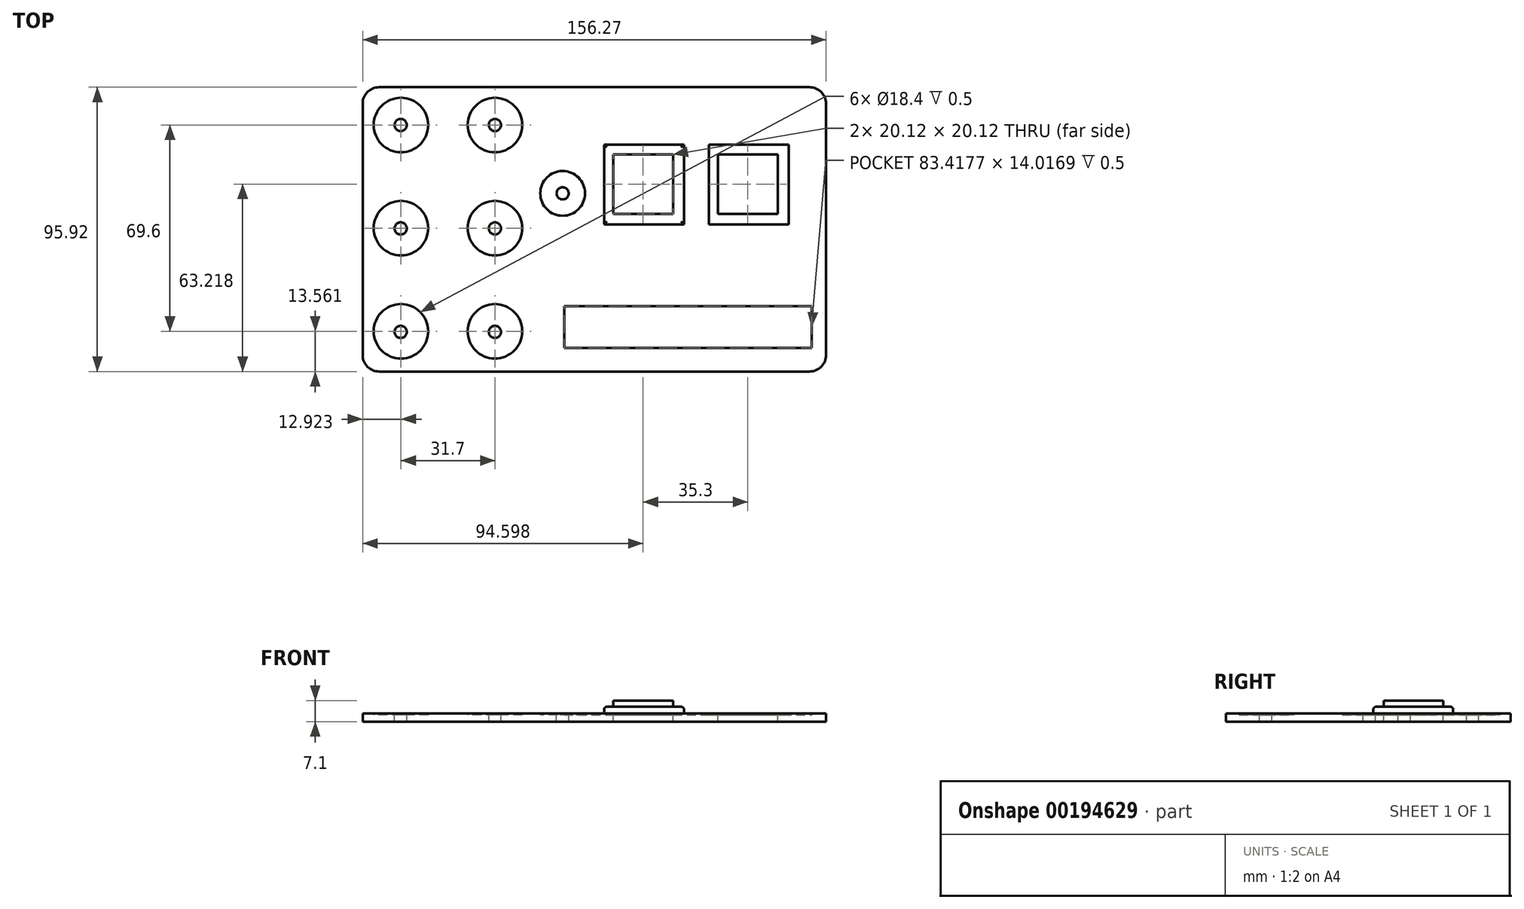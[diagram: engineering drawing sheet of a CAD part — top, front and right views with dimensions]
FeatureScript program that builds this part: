
annotation { "Feature Type Name" : "Feature", "Feature Type Description" : "" }
export const myFeature = defineFeature(function(context is Context, id is Id, definition is map)
    precondition{}
    {
        {
            var Q0;
            Q0=qCreatedBy(makeId("Top.planeOp"),FACE);
            var sketch = newSketch(context, id + "F0", { "sketchPlane" : qUnion([Q0])});
            skLineSegment(sketch, "E0.bottom", {"start": v(10.04, -4.66) * mm, "end": v(155.11, -4.66) * mm});
            skLineSegment(sketch, "E0.top", {"start": v(10.04, -100.58) * mm, "end": v(155.11, -100.58) * mm});
            skLineSegment(sketch, "E0.left", {"start": v(4.44, -10.26) * mm, "end": v(4.44, -94.98) * mm});
            skLineSegment(sketch, "E0.right", {"start": v(160.71, -10.26) * mm, "end": v(160.71, -94.98) * mm});
            skPoint(sketch, "E1.visualSharp", {"position": v(4.44, -4.66) * mm});
            skArc(sketch, "E1.filletArc", {"start": v(10.04, -4.66) * mm, "mid": v(6.08, -6.3) * mm, "end": v(4.44, -10.26) * mm});
            skPoint(sketch, "E2.visualSharp", {"position": v(4.44, -100.58) * mm});
            skArc(sketch, "E2.filletArc", {"start": v(4.44, -94.98) * mm, "mid": v(6.08, -98.94) * mm, "end": v(10.04, -100.58) * mm});
            skPoint(sketch, "E3.visualSharp", {"position": v(160.71, -100.58) * mm});
            skArc(sketch, "E3.filletArc", {"start": v(155.11, -100.58) * mm, "mid": v(159.07, -98.94) * mm, "end": v(160.71, -94.98) * mm});
            skPoint(sketch, "E4.visualSharp", {"position": v(160.71, -4.66) * mm});
            skArc(sketch, "E4.filletArc", {"start": v(160.71, -10.26) * mm, "mid": v(159.07, -6.3) * mm, "end": v(155.11, -4.66) * mm});
            skLineSegment(sketch, "E5.bottom", {"start": v(85.85, -50.95) * mm, "end": v(112.8, -50.95) * mm});
            skLineSegment(sketch, "E5.top", {"start": v(85.85, -24) * mm, "end": v(112.8, -24) * mm});
            skLineSegment(sketch, "E5.left", {"start": v(85.85, -50.95) * mm, "end": v(85.85, -24) * mm});
            skLineSegment(sketch, "E5.right", {"start": v(112.8, -50.95) * mm, "end": v(112.8, -24) * mm});
            skCircle(sketch, "E6", {"center": v(49.06, -17.42) * mm, "radius": 9.2 * mm});
            skPoint(sketch, "E6.first.point", {"position": v(44.08, -25.15) * mm});
            skPoint(sketch, "E6.second.point", {"position": v(45.09, -9.12) * mm});
            skPoint(sketch, "E6.third.point", {"position": v(58.27, -17.36) * mm});
            skLineSegment(sketch, "E7.bottom", {"start": v(88.98, -27.3) * mm, "end": v(109.1, -27.3) * mm});
            skLineSegment(sketch, "E7.top", {"start": v(88.98, -47.42) * mm, "end": v(109.1, -47.42) * mm});
            skLineSegment(sketch, "E7.left", {"start": v(88.98, -27.3) * mm, "end": v(88.98, -47.42) * mm});
            skLineSegment(sketch, "E7.right", {"start": v(109.1, -27.3) * mm, "end": v(109.1, -47.42) * mm});
            skLineSegment(sketch, "E8.1.0.0", {"start": v(121.15, -24) * mm, "end": v(148.1, -24) * mm});
            skLineSegment(sketch, "E8.1.0.1", {"start": v(121.15, -50.95) * mm, "end": v(121.15, -24) * mm});
            skLineSegment(sketch, "E8.1.0.2", {"start": v(121.15, -50.95) * mm, "end": v(148.1, -50.95) * mm});
            skLineSegment(sketch, "E8.1.0.3", {"start": v(148.1, -50.95) * mm, "end": v(148.1, -24) * mm});
            skLineSegment(sketch, "E8.1.0.4", {"start": v(144.4, -27.3) * mm, "end": v(144.4, -47.42) * mm});
            skLineSegment(sketch, "E8.1.0.5", {"start": v(124.28, -27.3) * mm, "end": v(144.4, -27.3) * mm});
            skLineSegment(sketch, "E8.1.0.6", {"start": v(124.28, -27.3) * mm, "end": v(124.28, -47.42) * mm});
            skLineSegment(sketch, "E8.1.0.7", {"start": v(124.28, -47.42) * mm, "end": v(144.4, -47.42) * mm});
            skLineSegment(sketch, "E8.direction1", {"start": v(85.85, -50.95) * mm, "end": v(121.15, -50.95) * mm, "construction": true});
            skCircle(sketch, "E9.0.1.0", {"center": v(49.06, -52.22) * mm, "radius": 9.2 * mm});
            skCircle(sketch, "E9.0.2.0", {"center": v(49.06, -87.02) * mm, "radius": 9.2 * mm});
            skCircle(sketch, "E9.1.0.0", {"center": v(17.36, -17.42) * mm, "radius": 9.2 * mm});
            skCircle(sketch, "E9.1.1.0", {"center": v(17.36, -52.22) * mm, "radius": 9.2 * mm});
            skCircle(sketch, "E9.1.2.0", {"center": v(17.36, -87.02) * mm, "radius": 9.2 * mm});
            skLineSegment(sketch, "E9.direction1", {"start": v(49.06, -17.42) * mm, "end": v(17.36, -17.42) * mm, "construction": true});
            skLineSegment(sketch, "E9.direction2", {"start": v(49.06, -17.42) * mm, "end": v(49.06, -52.22) * mm, "construction": true});
            skCircle(sketch, "E10", {"center": v(71.88, -40.48) * mm, "radius": 7.54 * mm});
            skPoint(sketch, "E10.first.point", {"position": v(67.34, -34.46) * mm});
            skPoint(sketch, "E10.second.point", {"position": v(72.06, -48.02) * mm});
            skPoint(sketch, "E10.third.point", {"position": v(79.37, -39.64) * mm});
            skLineSegment(sketch, "E11.bottom", {"start": v(72.42, -78.56) * mm, "end": v(155.84, -78.56) * mm});
            skLineSegment(sketch, "E11.top", {"start": v(72.42, -92.58) * mm, "end": v(155.84, -92.58) * mm});
            skLineSegment(sketch, "E11.left", {"start": v(72.42, -78.56) * mm, "end": v(72.42, -92.58) * mm});
            skLineSegment(sketch, "E11.right", {"start": v(155.84, -78.56) * mm, "end": v(155.84, -92.58) * mm});
            skLineSegment(sketch, "E12.0", {"start": v(7.94, -8.16) * mm, "end": v(157.21, -8.16) * mm});
            skLineSegment(sketch, "E12.1", {"start": v(7.94, -8.16) * mm, "end": v(7.94, -97.08) * mm});
            skLineSegment(sketch, "E12.2", {"start": v(7.94, -97.08) * mm, "end": v(157.21, -97.08) * mm});
            skLineSegment(sketch, "E12.3", {"start": v(157.21, -8.16) * mm, "end": v(157.21, -97.08) * mm});
            skCircle(sketch, "E13", {"center": v(49.06, -17.42) * mm, "radius": 2.05 * mm});
            skCircle(sketch, "E14.0.1.0", {"center": v(49.06, -52.32) * mm, "radius": 2.05 * mm});
            skCircle(sketch, "E14.0.2.0", {"center": v(49.06, -87.22) * mm, "radius": 2.05 * mm});
            skCircle(sketch, "E14.1.0.0", {"center": v(17.26, -17.42) * mm, "radius": 2.05 * mm});
            skCircle(sketch, "E14.1.1.0", {"center": v(17.26, -52.32) * mm, "radius": 2.05 * mm});
            skCircle(sketch, "E14.1.2.0", {"center": v(17.26, -87.22) * mm, "radius": 2.05 * mm});
            skLineSegment(sketch, "E14.direction1", {"start": v(49.06, -17.42) * mm, "end": v(17.26, -17.42) * mm, "construction": true});
            skLineSegment(sketch, "E14.direction2", {"start": v(49.06, -17.42) * mm, "end": v(49.06, -52.32) * mm, "construction": true});
            skCircle(sketch, "E15", {"center": v(71.88, -40.48) * mm, "radius": 2.05 * mm});
            skSolve(sketch);
        }
        {
            var Q0;
            Q0=makeQuery(id+"F0.imprint","IMPRINT",FACE,{"disambiguationData":[TD([[makeQuery(id+"F0.imprint","IMPRINT",EDGE,{"derivedFrom":sQuery(id+"F0.wireOp",EDGE,"E0.bottom")}),-1.0]])]});
            var Q1;
            Q1=makeQuery(id+"F0.imprint","IMPRINT",FACE,{"disambiguationData":[TD([[makeQuery(id+"F0.imprint","IMPRINT",EDGE,{"derivedFrom":sQuery(id+"F0.wireOp",EDGE,"E5.bottom")}),-1.0]])]});
            var Q2;
            Q2=makeQuery(id+"F0.imprint","IMPRINT",FACE,{"disambiguationData":[TD([[makeQuery(id+"F0.imprint","IMPRINT",EDGE,{"derivedFrom":sQuery(id+"F0.wireOp",EDGE,"E9.1.0.0")}),1.0]])]});
            var Q3;
            Q3=makeQuery(id+"F0.imprint","IMPRINT",FACE,{"disambiguationData":[TD([[makeQuery(id+"F0.imprint","IMPRINT",EDGE,{"derivedFrom":sQuery(id+"F0.wireOp",EDGE,"E9.1.1.0")}),1.0]])]});
            var Q4;
            Q4=makeQuery(id+"F0.imprint","IMPRINT",FACE,{"disambiguationData":[TD([[makeQuery(id+"F0.imprint","IMPRINT",EDGE,{"derivedFrom":sQuery(id+"F0.wireOp",EDGE,"E9.1.2.0")}),1.0]])]});
            var Q5;
            Q5=makeQuery(id+"F0.imprint","IMPRINT",FACE,{"disambiguationData":[TD([[makeQuery(id+"F0.imprint","IMPRINT",EDGE,{"derivedFrom":sQuery(id+"F0.wireOp",EDGE,"E9.0.2.0")}),1.0]])]});
            var Q6;
            Q6=makeQuery(id+"F0.imprint","IMPRINT",FACE,{"disambiguationData":[TD([[makeQuery(id+"F0.imprint","IMPRINT",EDGE,{"derivedFrom":sQuery(id+"F0.wireOp",EDGE,"E9.0.1.0")}),1.0]])]});
            var Q7;
            Q7=makeQuery(id+"F0.imprint","IMPRINT",FACE,{"disambiguationData":[TD([[makeQuery(id+"F0.imprint","IMPRINT",EDGE,{"derivedFrom":sQuery(id+"F0.wireOp",EDGE,"E6")}),1.0]])]});
            var Q8;
            Q8=makeQuery(id+"F0.imprint","IMPRINT",FACE,{"disambiguationData":[TD([[makeQuery(id+"F0.imprint","IMPRINT",EDGE,{"derivedFrom":sQuery(id+"F0.wireOp",EDGE,"E10")}),1.0]])]});
            var Q9;
            Q9=makeQuery(id+"F0.imprint","IMPRINT",FACE,{"disambiguationData":[TD([[makeQuery(id+"F0.imprint","IMPRINT",EDGE,{"derivedFrom":sQuery(id+"F0.wireOp",EDGE,"E11.bottom")}),-1.0]])]});
            var Q10;
            Q10=makeQuery(id+"F0.imprint","IMPRINT",FACE,{"disambiguationData":[TD([[makeQuery(id+"F0.imprint","IMPRINT",EDGE,{"derivedFrom":sQuery(id+"F0.wireOp",EDGE,"E5.bottom")}),1.0]])]});
            var Q11;
            Q11=makeQuery(id+"F0.imprint","IMPRINT",FACE,{"disambiguationData":[TD([[makeQuery(id+"F0.imprint","IMPRINT",EDGE,{"derivedFrom":sQuery(id+"F0.wireOp",EDGE,"E8.1.0.0")}),-1.0]])]});
            extrude(context, id + "F1", {"entities" : qUnion([Q0, Q1, Q2, Q3, Q4, Q5, Q6, Q7, Q8, Q9, Q10, Q11]), "oppositeDirection" : true, "depth" : 2.2 * mm});
        }
        {
            var Q0;
            Q0=makeQuery(id+"F0.imprint","IMPRINT",FACE,{"disambiguationData":[TD([[makeQuery(id+"F0.imprint","IMPRINT",EDGE,{"derivedFrom":sQuery(id+"F0.wireOp",EDGE,"E0.bottom")}),-1.0]])]});
            var Q1;
            Q1=makeQuery(id+"F0.imprint","IMPRINT",FACE,{"disambiguationData":[TD([[makeQuery(id+"F0.imprint","IMPRINT",EDGE,{"derivedFrom":sQuery(id+"F0.wireOp",EDGE,"E5.bottom")}),-1.0]])]});
            extrude(context, id + "F2", {"entities" : qUnion([Q0, Q1]), "operationType" : NewBodyOperationType.ADD, "depth" : .5 * mm});
        }
        {
            var Q0;
            Q0=makeQuery(id+"F0.imprint","IMPRINT",FACE,{"disambiguationData":[TD([[makeQuery(id+"F0.imprint","IMPRINT",EDGE,{"derivedFrom":sQuery(id+"F0.wireOp",EDGE,"E5.bottom")}),1.0]])]});
            extrude(context, id + "F3", {"entities" : qUnion([Q0]), "depth" : 2.8 * mm});
        }
        {
            var Q0;
            Q0=makeQuery(id+"F3.opExtrude","CAP_EDGE",EDGE,{"disambiguationData":[OSD([sQuery(id+"F0.wireOp",EDGE,"E5.bottom")])],"isStart":false});
            var Q1;
            Q1=makeQuery(id+"F3.opExtrude","CAP_EDGE",EDGE,{"disambiguationData":[OSD([sQuery(id+"F0.wireOp",EDGE,"E5.left")])],"isStart":false});
            var Q2;
            Q2=makeQuery(id+"F3.opExtrude","CAP_EDGE",EDGE,{"disambiguationData":[OSD([sQuery(id+"F0.wireOp",EDGE,"E5.top")])],"isStart":false});
            var Q3;
            Q3=makeQuery(id+"F3.opExtrude","CAP_EDGE",EDGE,{"disambiguationData":[OSD([sQuery(id+"F0.wireOp",EDGE,"E5.right")])],"isStart":false});
            fillet(context, id + "F4", {"entities" : qUnion([Q0, Q1, Q2, Q3]), "radius" : 1 * mm, "tangentPropagation" : true, "allowEdgeOverflow" : false});
        }
        {
            var Q0;
            Q0=makeQuery(id+"F0.imprint","IMPRINT",FACE,{"disambiguationData":[TD([[makeQuery(id+"F0.imprint","IMPRINT",EDGE,{"derivedFrom":sQuery(id+"F0.wireOp",EDGE,"E7.bottom")}),-1.0]])]});
            extrude(context, id + "F5", {"entities" : qUnion([Q0]), "operationType" : NewBodyOperationType.ADD, "depth" : 4.9 * mm});
        }
    });
